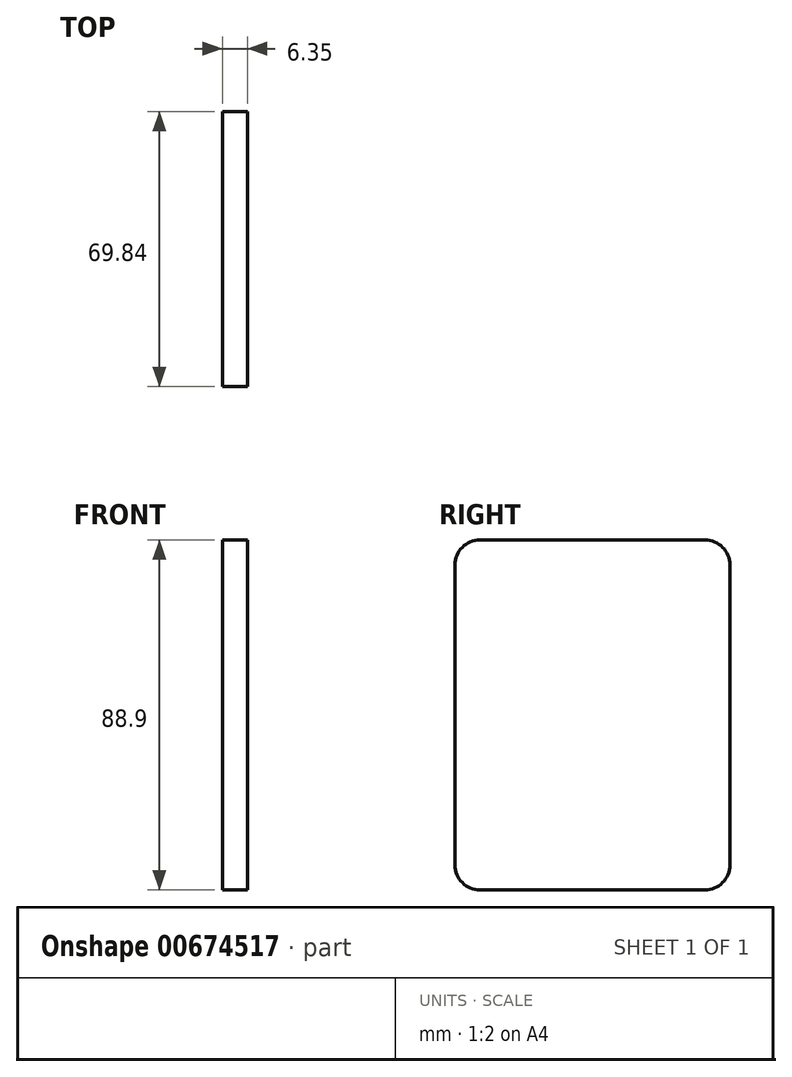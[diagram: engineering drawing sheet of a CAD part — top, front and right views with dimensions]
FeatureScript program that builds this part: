
annotation { "Feature Type Name" : "Feature", "Feature Type Description" : "" }
export const myFeature = defineFeature(function(context is Context, id is Id, definition is map)
    precondition{}
    {
        {
            var Q0;
            Q0=qCreatedBy(makeId("Right.planeOp"),FACE);
            var sketch = newSketch(context, id + "F0", { "sketchPlane" : qUnion([Q0])});
            skLineSegment(sketch, "E0.bottom", {"start": v(31.75, 47.63) * mm, "end": v(-31.75, 47.63) * mm});
            skLineSegment(sketch, "E0.top", {"start": v(31.75, -47.62) * mm, "end": v(-31.75, -47.62) * mm});
            skLineSegment(sketch, "E0.left", {"start": v(41.28, 38.1) * mm, "end": v(41.28, -38.1) * mm});
            skLineSegment(sketch, "E0.right", {"start": v(-41.27, 38.1) * mm, "end": v(-41.27, -38.1) * mm});
            skPoint(sketch, "E0.middle", {"position": v(0, 0) * mm});
            skPoint(sketch, "E1.visualSharp", {"position": v(41.28, 47.63) * mm});
            skArc(sketch, "E1.filletArc", {"start": v(41.28, 38.1) * mm, "mid": v(38.49, 44.84) * mm, "end": v(31.75, 47.63) * mm});
            skPoint(sketch, "E2.visualSharp", {"position": v(-41.27, 47.63) * mm});
            skArc(sketch, "E2.filletArc", {"start": v(-31.75, 47.63) * mm, "mid": v(-38.49, 44.84) * mm, "end": v(-41.27, 38.1) * mm});
            skPoint(sketch, "E3.visualSharp", {"position": v(41.27, -47.62) * mm});
            skArc(sketch, "E3.filletArc", {"start": v(31.75, -47.63) * mm, "mid": v(38.49, -44.84) * mm, "end": v(41.28, -38.1) * mm});
            skPoint(sketch, "E4.visualSharp", {"position": v(-41.28, -47.62) * mm});
            skArc(sketch, "E4.filletArc", {"start": v(-41.28, -38.1) * mm, "mid": v(-38.49, -44.84) * mm, "end": v(-31.75, -47.63) * mm});
            skSolve(sketch);
        }
        {
            var Q0;
            Q0 = qSketchRegion(id + "F0", true);
            extrude(context, id + "F1", {"entities" : qUnion([Q0]), "depth" : 6.35 * mm, "offsetDistance" : 25.4 * mm});
        }
        {
            var Q0;
            Q0=makeQuery(id+"F1.opExtrude","SWEPT_BODY",BODY,{"disambiguationData":[OSD([sQuery(id+"F0.wireOp",EDGE,"E0.bottom"),sQuery(id+"F0.wireOp",EDGE,"E0.top"),sQuery(id+"F0.wireOp",EDGE,"E0.left"),sQuery(id+"F0.wireOp",EDGE,"E0.right"),sQuery(id+"F0.wireOp",EDGE,"E1.filletArc"),sQuery(id+"F0.wireOp",EDGE,"E2.filletArc"),sQuery(id+"F0.wireOp",EDGE,"E3.filletArc"),sQuery(id+"F0.wireOp",EDGE,"E4.filletArc")])]});
            deleteBodies(context, id + "F2", {"entities" : qUnion([Q0])});
        }
        {
            var Q0;
            Q0=qCreatedBy(makeId("Right.planeOp"),FACE);
            var sketch = newSketch(context, id + "F3", { "sketchPlane" : qUnion([Q0])});
            skLineSegment(sketch, "E5.bottom", {"start": v(28.58, 44.45) * mm, "end": v(-28.58, 44.45) * mm});
            skLineSegment(sketch, "E5.top", {"start": v(28.57, -44.45) * mm, "end": v(-28.58, -44.45) * mm});
            skLineSegment(sketch, "E5.left", {"start": v(34.92, 38.1) * mm, "end": v(34.92, -38.1) * mm});
            skLineSegment(sketch, "E5.right", {"start": v(-34.93, 38.1) * mm, "end": v(-34.93, -38.1) * mm});
            skPoint(sketch, "E5.middle", {"position": v(0, 0) * mm});
            skPoint(sketch, "E6.visualSharp", {"position": v(34.93, 44.45) * mm});
            skArc(sketch, "E6.filletArc", {"start": v(34.93, 38.1) * mm, "mid": v(33.07, 42.6) * mm, "end": v(28.58, 44.45) * mm});
            skPoint(sketch, "E7.visualSharp", {"position": v(34.92, -44.45) * mm});
            skArc(sketch, "E7.filletArc", {"start": v(28.57, -44.45) * mm, "mid": v(33.07, -42.6) * mm, "end": v(34.92, -38.1) * mm});
            skPoint(sketch, "E8.visualSharp", {"position": v(-34.93, -44.45) * mm});
            skArc(sketch, "E8.filletArc", {"start": v(-34.93, -38.1) * mm, "mid": v(-33.07, -42.6) * mm, "end": v(-28.58, -44.45) * mm});
            skPoint(sketch, "E9.visualSharp", {"position": v(-34.92, 44.45) * mm});
            skArc(sketch, "E9.filletArc", {"start": v(-28.58, 44.45) * mm, "mid": v(-33.07, 42.6) * mm, "end": v(-34.93, 38.1) * mm});
            skSolve(sketch);
        }
        {
            var Q0;
            Q0 = qSketchRegion(id + "F3", true);
            extrude(context, id + "F4", {"entities" : qUnion([Q0]), "depth" : 6.35 * mm, "offsetDistance" : 25.4 * mm});
        }
    });
